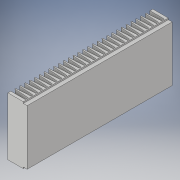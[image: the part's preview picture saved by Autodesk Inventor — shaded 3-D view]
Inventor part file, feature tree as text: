
AUTODESK INVENTOR PART (.ipt)
format: ipt  version: 2019 (Build 230136000, 136)  size: 319,488 bytes
history: native  units: mm
features: extrude x4, sketch x4, projected_geometry x2, other x1, pattern_linear x1
ambient origin geometry x8: Origin, YZ Plane, XZ Plane, XY Plane, X Axis, Y Axis, Z Axis, Center Point
bodies: Body1 (feature_tree)
feature tree (12):
  other  "Těleso1"
  extrude  "Vysunutí1"  Depth=40.0mm
  extrude  "Vysunutí2"  Depth=6.0mm
  pattern_linear  "Obdélníkové pole1"  Spacing1=2.5mm  [1 undecoded]
  extrude  "Vysunutí3"  Depth=10.0mm
  extrude  "Vysunutí6"  Depth=15.0mm
  sketch  "Náčrt1"
  sketch  "Náčrt2"
  projected_geometry  "Promítnutá smyčka1"
  sketch  "Náčrt3"
  projected_geometry  "Promítnutá smyčka2"
  sketch  "Náčrt4"
note: 1 required parameter value undecoded (feature->parameter linkage not recoverable at this tier; creation-order binding heuristic only, values carry confidence <= 0.55)
